# Revit family: Haworth_Planes_HeightAdjustTable_90-WrapAround
name_source: partatom
category: Furniture Systems
revit_build: Autodesk Revit 2018 (Build: 20170223_1515(x64)
units: mm (PartAtom-declared; Revit-internal decimal feet)

## family parameters
Always vertical = Yes
Cut with Voids When Loaded = No
OmniClass Number = 23.40.70.14.64.21
OmniClass Title = Systems Furniture
Part Type = Normal
Room Calculation Point = No
Round Connector Dimension = Use Diameter
Shared = No
Work Plane-Based = No

## types (3) — shared parameters
23 Deep = Yes
Actual Depth = 23"
Actual Height = 40"
Assembly Code = E2020200
Base Tube Finish = Haworth _ Paint _ Smoke
Custom Size = No
Depth = 23"
Edgeband = Yes
Height = 40"
Knife Edge = No
Manufacturer = Haworth
Max. Depth = 23"
Max. Height = 46"
Max. Width = 46"
Min. Depth = 23"
Min. Height = 27"
Min. Width = 34"
Min/Max Depth = 23 in.
Min/Max Width = 34, 40, 46 in.
Model = TACR
Radius = 10 1/4"
Radius 2 = 12 1/4"
Revision Number = 1
Size = Verify Final Dim. w/ Haworth
Support Height = 38 13/16"
Top Thickness = 1 3/16"
URL = www.haworth.com
URL - Product = https://www.haworth.com
Warranty = http://www.haworth.com

## per-type parameters (varying)
| type | Actual Width | Back Start Control | Description | Leg Back Offset | Leg Side Offset | Width |
| 40w 23d | 40" | 5 83/128" | Haworth Planes - HAT - 90 Wrap Around - 40w 23d | 16 31/32" | 14" | 40" |
| 34w 23d | 34" | 4 1/4" | Haworth Planes - HAT - 90 Wrap Around - 34w 23d | 14 11/32" | 11 1/2" | 34" |
| 46w 23d | 46" | 5 83/128" | Haworth Planes - HAT - 90 Wrap Around - 46w 23d | 18 5/32" | 17" | 46" |

## geometry (parser evidence)
native form markers: Sweep x9
no freeform markers — native parametric forms only
